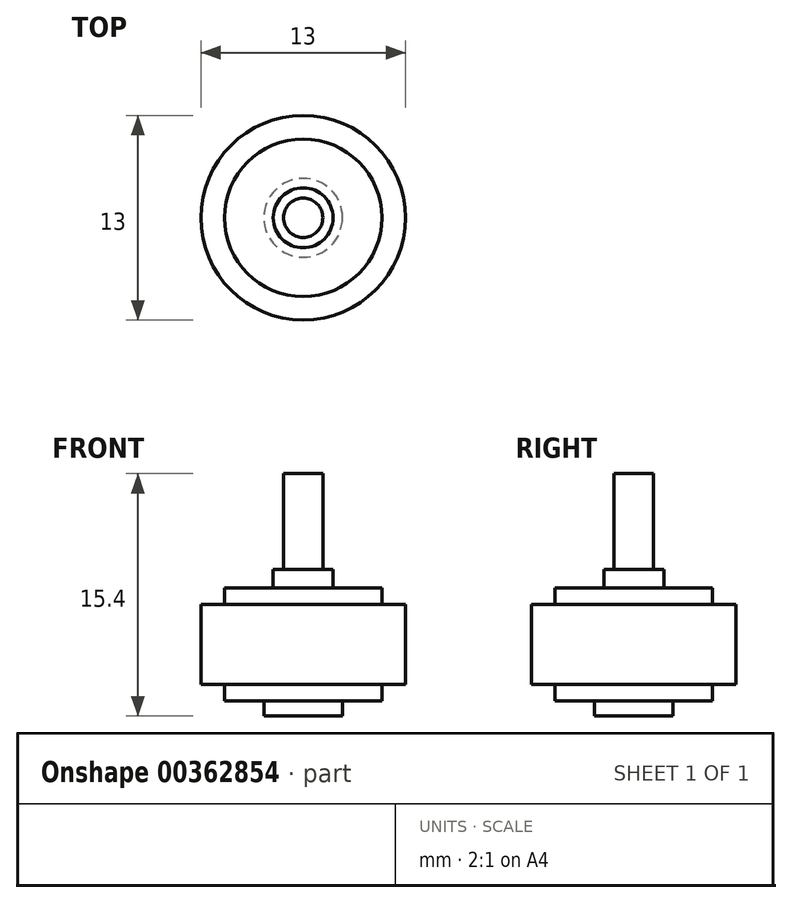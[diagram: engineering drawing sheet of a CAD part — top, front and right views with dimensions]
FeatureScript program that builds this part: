
annotation { "Feature Type Name" : "Feature", "Feature Type Description" : "" }
export const myFeature = defineFeature(function(context is Context, id is Id, definition is map)
    precondition{}
    {
        {
            var Q0;
            Q0=qCreatedBy(makeId("Top.planeOp"),FACE);
            var sketch = newSketch(context, id + "F0", { "sketchPlane" : qUnion([Q0])});
            skCircle(sketch, "E0", {"center": v(0, 0) * mm, "radius": 6.5 * mm});
            skSolve(sketch);
        }
        {
            var Q0;
            Q0=makeQuery(id+"F0.imprint","IMPRINT",FACE,{"disambiguationData":[TD([[makeQuery(id+"F0.imprint","IMPRINT",EDGE,{"derivedFrom":sQuery(id+"F0.wireOp",EDGE,"E0")}),1.0]])]});
            extrude(context, id + "F1", {"entities" : qUnion([Q0]), "depth" : 5.1 * mm});
        }
        {
            var Q0;
            Q0=qCreatedBy(makeId("Top.planeOp"),FACE);
            var sketch = newSketch(context, id + "F2", { "sketchPlane" : qUnion([Q0])});
            skCircle(sketch, "E1", {"center": v(0, 0) * mm, "radius": 5 * mm});
            skSolve(sketch);
        }
        {
            var Q0;
            Q0 = qSketchRegion(id + "F2", true);
            extrude(context, id + "F3", {"entities" : qUnion([Q0]), "operationType" : NewBodyOperationType.ADD, "depth" : 6.15 * mm, "hasSecondDirection" : true, "secondDirectionOppositeDirection" : true, "secondDirectionDepth" : 1.05 * mm});
        }
        {
            var Q0;
            Q0=qCreatedBy(makeId("Top.planeOp"),FACE);
            var sketch = newSketch(context, id + "F4", { "sketchPlane" : qUnion([Q0])});
            skCircle(sketch, "E2", {"center": v(0, 0) * mm, "radius": 1.9 * mm});
            skSolve(sketch);
        }
        {
            var Q0;
            Q0 = qSketchRegion(id + "F4", true);
            extrude(context, id + "F5", {"entities" : qUnion([Q0]), "operationType" : NewBodyOperationType.ADD, "depth" : 7.3 * mm});
        }
        {
            var Q0;
            Q0=qCreatedBy(makeId("Top.planeOp"),FACE);
            var sketch = newSketch(context, id + "F6", { "sketchPlane" : qUnion([Q0])});
            skCircle(sketch, "E3", {"center": v(0, 0) * mm, "radius": 2.5 * mm});
            skSolve(sketch);
        }
        {
            var Q0;
            Q0 = qSketchRegion(id + "F6", true);
            extrude(context, id + "F7", {"entities" : qUnion([Q0]), "operationType" : NewBodyOperationType.ADD, "oppositeDirection" : true, "depth" : 2 * mm});
        }
        {
            var Q0;
            Q0=qCreatedBy(makeId("Top.planeOp"),FACE);
            var sketch = newSketch(context, id + "F8", { "sketchPlane" : qUnion([Q0])});
            skCircle(sketch, "E4", {"center": v(0, 0) * mm, "radius": 1.25 * mm});
            skSolve(sketch);
        }
        {
            var Q0;
            Q0 = qSketchRegion(id + "F8", true);
            extrude(context, id + "F9", {"entities" : qUnion([Q0]), "operationType" : NewBodyOperationType.ADD, "depth" : 13.4 * mm});
        }
    });
